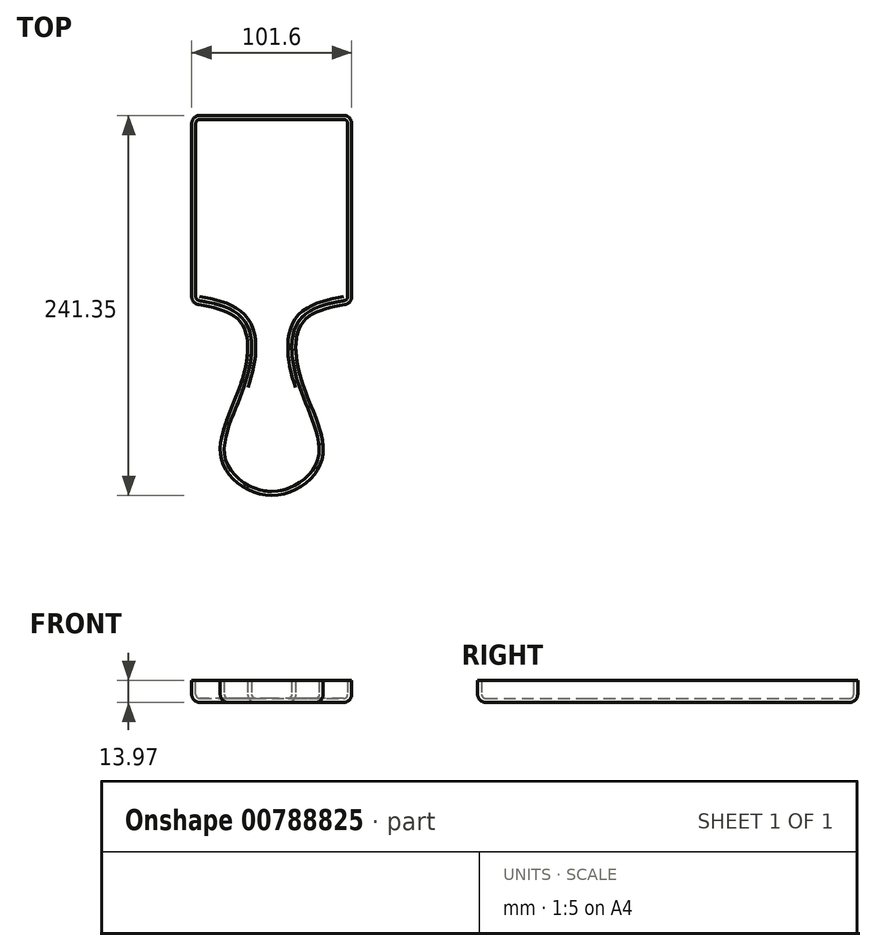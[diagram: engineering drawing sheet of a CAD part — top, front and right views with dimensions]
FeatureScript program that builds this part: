
annotation { "Feature Type Name" : "Feature", "Feature Type Description" : "" }
export const myFeature = defineFeature(function(context is Context, id is Id, definition is map)
    precondition{}
    {
        {
            var Q0;
            Q0=qCreatedBy(makeId("Top.planeOp"),FACE);
            var sketch = newSketch(context, id + "F0", { "sketchPlane" : qUnion([Q0])});
            skLineSegment(sketch, "E0.top", {"start": v(-50.8, -59.7) * mm, "end": v(50.8, -59.7) * mm});
            skLineSegment(sketch, "E1.bottom", {"start": v(-19.05, -59.7) * mm, "end": v(19.05, -59.7) * mm});
            skLineSegment(sketch, "E1.top", {"start": v(-19.05, -143.51) * mm, "end": v(19.05, -143.51) * mm});
            skLineSegment(sketch, "E2", {"start": v(-19.05, -59.69) * mm, "end": v(-138.22, -148.68) * mm, "construction": true});
            skPoint(sketch, "E3.4.internal.snap0", {"position": v(0, -143.51) * mm});
            skFitSpline(sketch, "E4", {"points": [v(31.98, -161.28) * mm, v(-138.22, -161.28) * mm], "startDerivative": vector(-191.75, -9.7) * mm, "endDerivative": vector(-168.23, 0) * mm, "construction": true});
            skFitSpline(sketch, "E5", {"points": [v(19.04, -111.52) * mm, v(-199.9, -111.52) * mm], "startDerivative": vector(-218.94, 0) * mm, "endDerivative": vector(-218.94, 0) * mm, "construction": true});
            skLineSegment(sketch, "E6", {"start": v(50.8, -59.7) * mm, "end": v(50.8, -228.04) * mm, "construction": true});
            skLineSegment(sketch, "E7", {"start": v(-50.8, -59.7) * mm, "end": v(-50.8, -228.04) * mm, "construction": true});
            skPoint(sketch, "E8", {"position": v(-44.45, -162.64) * mm});
            skPoint(sketch, "E9", {"position": v(31.8, -161.3) * mm});
            skLineSegment(sketch, "E10", {"start": v(0, -228.04) * mm, "end": v(0, -135.28) * mm});
            skPoint(sketch, "E11.orphan", {"position": v(0, -221.87) * mm});
            skLineSegment(sketch, "E12", {"start": v(-50.8, -59.7) * mm, "end": v(-50.8, 59.69) * mm});
            skLineSegment(sketch, "E13", {"start": v(-50.8, 59.69) * mm, "end": v(50.8, 59.69) * mm});
            skLineSegment(sketch, "E14", {"start": v(50.8, 59.69) * mm, "end": v(50.8, -59.7) * mm});
            skLineSegment(sketch, "E15", {"start": v(0, -59.7) * mm, "end": v(0, 0) * mm, "construction": true});
            skFitSpline(sketch, "E16", {"points": [v(19.04, -111.52) * mm, v(-199.9, -111.52) * mm], "startDerivative": vector(-218.94, 0) * mm, "endDerivative": vector(-218.94, 0) * mm, "construction": true});
            skFitSpline(sketch, "E17", {"points": [v(-50.8, -59.7) * mm, v(-19.83, -71.53) * mm, v(-19.05, -108.97) * mm, v(-31.95, -158.73) * mm, v(0, -181.66) * mm, v(31.95, -158.73) * mm, v(19.05, -108.97) * mm, v(19.83, -71.53) * mm, v(50.8, -59.7) * mm], "startDerivative": vector(328.9, -55.01) * mm, "endDerivative": vector(328.9, 55.01) * mm});
            skFitSpline(sketch, "E18.MirrorCS", {"points": [v(50.8, -59.7) * mm, v(19.83, -71.53) * mm, v(19.05, -108.97) * mm, v(31.95, -158.73) * mm, v(0, -181.66) * mm, v(-31.95, -158.73) * mm, v(-19.05, -108.97) * mm, v(-19.83, -71.53) * mm, v(-50.8, -59.7) * mm], "startDerivative": vector(-328.9, -55.01) * mm, "endDerivative": vector(-328.9, 55.01) * mm});
            skFitSpline(sketch, "E19", {"points": [v(-20.16, -129.65) * mm, v(-15.25, -116.48) * mm, v(-19.9, -111.52) * mm], "startDerivative": vector(14.14, 25.35) * mm, "endDerivative": vector(-15.4, 9.99) * mm});
            skFitSpline(sketch, "E20.MirrorCS", {"points": [v(20.16, -129.65) * mm, v(15.25, -116.48) * mm, v(19.9, -111.52) * mm], "startDerivative": vector(-14.14, 25.35) * mm, "endDerivative": vector(15.4, 9.99) * mm});
            skArc(sketch, "E21", {"start": v(-20.16, -129.65) * mm, "mid": v(0, -167.4) * mm, "end": v(20.16, -129.65) * mm});
            skLineSegment(sketch, "E22", {"start": v(-15.25, -116.48) * mm, "end": v(-15.25, -59.7) * mm});
            skSolve(sketch);
        }
        {
            var Q0;
            Q0 = qSketchRegion(id + "F0", true);
            extrude(context, id + "F1", {"entities" : qUnion([Q0]), "depth" : 19.05 * mm, "offsetDistance" : 25.4 * mm});
        }
        {
            var Q0;
            Q0=makeQuery(id+"F1.opExtrude","CAP_EDGE",EDGE,{"disambiguationData":[OSD([sQuery(id+"F0.wireOp",EDGE,"E0.left")])],"isStart":false});
            var Q1;
            {var subQ0=sQuery(id+"F0.wireOp",EDGE,"E0.top");Q1=makeQuery(id+"F1.opExtrude","CAP_EDGE",EDGE,{"disambiguationData":[OSD([subQ0]),TDD([makeQuery(id+"F0.imprint","IMPRINT",EDGE,{"disambiguationData":[TD([[makeQuery(id+"F0.imprint","INTERSECT",VERTEX,{"derivedFrom":[subQ0,sQuery(id+"F0.wireOp",EDGE,"E0.left")]}),-1.0]])],"derivedFrom":subQ0})])],"isStart":false});}
            var Q2;
            {var subQ0=sQuery(id+"F0.wireOp",EDGE,"E0.top");Q2=makeQuery(id+"F1.opExtrude","CAP_EDGE",EDGE,{"disambiguationData":[OSD([subQ0]),TDD([makeQuery(id+"F0.imprint","IMPRINT",EDGE,{"disambiguationData":[TD([[makeQuery(id+"F0.imprint","INTERSECT",VERTEX,{"derivedFrom":[subQ0,sQuery(id+"F0.wireOp",EDGE,"E0.left")]}),-1.0]])],"derivedFrom":subQ0})])],"isStart":true});}
            var Q3;
            Q3=makeQuery(id+"F1.opExtrude","CAP_EDGE",EDGE,{"disambiguationData":[OSD([sQuery(id+"F0.wireOp",EDGE,"E0.left")])],"isStart":true});
            var Q4;
            Q4=makeQuery(id+"F1.opExtrude","SWEPT_EDGE",EDGE,{"disambiguationData":[OSD([sQuery(id+"F0.wireOp",EDGE,"E0.top"),sQuery(id+"F0.wireOp",EDGE,"E0.left")])]});
            var Q5;
            Q5=makeQuery(id+"F1.opExtrude","SWEPT_EDGE",EDGE,{"disambiguationData":[OSD([sQuery(id+"F0.wireOp",EDGE,"E0.top"),sQuery(id+"F0.wireOp",EDGE,"E1.bottom"),sQuery(id+"F0.wireOp",EDGE,"E1.left")])]});
            var Q6;
            Q6=makeQuery(id+"F1.opExtrude","CAP_EDGE",EDGE,{"disambiguationData":[OSD([sQuery(id+"F0.wireOp",EDGE,"E0.bottom")])],"isStart":false});
            var Q7;
            Q7=makeQuery(id+"F1.opExtrude","CAP_EDGE",EDGE,{"disambiguationData":[OSD([sQuery(id+"F0.wireOp",EDGE,"E0.right")])],"isStart":false});
            var Q8;
            {var subQ0=sQuery(id+"F0.wireOp",EDGE,"E0.top");Q8=makeQuery(id+"F1.opExtrude","CAP_EDGE",EDGE,{"disambiguationData":[OSD([subQ0]),TDD([makeQuery(id+"F0.imprint","IMPRINT",EDGE,{"disambiguationData":[TD([[makeQuery(id+"F0.imprint","INTERSECT",VERTEX,{"derivedFrom":[subQ0,sQuery(id+"F0.wireOp",EDGE,"E0.right")]}),1.0]])],"derivedFrom":subQ0})])],"isStart":false});}
            var Q9;
            Q9=makeQuery(id+"F1.opExtrude","CAP_EDGE",EDGE,{"disambiguationData":[OSD([sQuery(id+"F0.wireOp",EDGE,"E1.right")])],"isStart":false});
            var Q10;
            Q10=makeQuery(id+"F1.opExtrude","CAP_EDGE",EDGE,{"disambiguationData":[OSD([sQuery(id+"F0.wireOp",EDGE,"E1.top")])],"isStart":false});
            var Q11;
            Q11=makeQuery(id+"F1.opExtrude","SWEPT_EDGE",EDGE,{"disambiguationData":[OSD([sQuery(id+"F0.wireOp",EDGE,"E1.top"),sQuery(id+"F0.wireOp",EDGE,"E1.right")])]});
            var Q12;
            Q12=makeQuery(id+"F1.opExtrude","SWEPT_EDGE",EDGE,{"disambiguationData":[OSD([sQuery(id+"F0.wireOp",EDGE,"E1.top"),sQuery(id+"F0.wireOp",EDGE,"E1.left")])]});
            var Q13;
            Q13=makeQuery(id+"F1.opExtrude","SWEPT_EDGE",EDGE,{"disambiguationData":[OSD([sQuery(id+"F0.wireOp",EDGE,"E0.top"),sQuery(id+"F0.wireOp",EDGE,"E1.bottom"),sQuery(id+"F0.wireOp",EDGE,"E1.right")])]});
            var Q14;
            Q14=makeQuery(id+"F1.opExtrude","SWEPT_EDGE",EDGE,{"disambiguationData":[OSD([sQuery(id+"F0.wireOp",EDGE,"E0.top"),sQuery(id+"F0.wireOp",EDGE,"E0.right")])]});
            var Q15;
            Q15=makeQuery(id+"F1.opExtrude","SWEPT_EDGE",EDGE,{"disambiguationData":[OSD([sQuery(id+"F0.wireOp",EDGE,"E0.bottom"),sQuery(id+"F0.wireOp",EDGE,"E0.right")])]});
            var Q16;
            Q16=makeQuery(id+"F1.opExtrude","CAP_EDGE",EDGE,{"disambiguationData":[OSD([sQuery(id+"F0.wireOp",EDGE,"E0.right")])],"isStart":true});
            var Q17;
            {var subQ0=sQuery(id+"F0.wireOp",EDGE,"E0.top");Q17=makeQuery(id+"F1.opExtrude","CAP_EDGE",EDGE,{"disambiguationData":[OSD([subQ0]),TDD([makeQuery(id+"F0.imprint","IMPRINT",EDGE,{"disambiguationData":[TD([[makeQuery(id+"F0.imprint","INTERSECT",VERTEX,{"derivedFrom":[subQ0,sQuery(id+"F0.wireOp",EDGE,"E0.right")]}),1.0]])],"derivedFrom":subQ0})])],"isStart":true});}
            var Q18;
            Q18=makeQuery(id+"F1.opExtrude","CAP_EDGE",EDGE,{"disambiguationData":[OSD([sQuery(id+"F0.wireOp",EDGE,"E1.right")])],"isStart":true});
            var Q19;
            Q19=makeQuery(id+"F1.opExtrude","CAP_EDGE",EDGE,{"disambiguationData":[OSD([sQuery(id+"F0.wireOp",EDGE,"E1.top")])],"isStart":true});
            var Q20;
            Q20=makeQuery(id+"F1.opExtrude","CAP_EDGE",EDGE,{"disambiguationData":[OSD([sQuery(id+"F0.wireOp",EDGE,"E0.bottom")])],"isStart":true});
            var Q21;
            Q21=makeQuery(id+"F1.opExtrude","SWEPT_EDGE",EDGE,{"disambiguationData":[OSD([sQuery(id+"F0.wireOp",EDGE,"E0.bottom"),sQuery(id+"F0.wireOp",EDGE,"E0.left")])]});
            var Q22;
            Q22=makeQuery(id+"F1.opExtrude","CAP_EDGE",EDGE,{"disambiguationData":[OSD([sQuery(id+"F0.wireOp",EDGE,"4c1d50d4-069b-4383-b718-4d861729b4e2")])],"isStart":false});
            var Q23;
            Q23=makeQuery(id+"F1.opExtrude","CAP_EDGE",EDGE,{"disambiguationData":[OSD([sQuery(id+"F0.wireOp",EDGE,"4c1d50d4-069b-4383-b718-4d861729b4e2")])],"isStart":true});
            var Q24;
            Q24=makeQuery(id+"F1.opExtrude","CAP_EDGE",EDGE,{"disambiguationData":[OSD([sQuery(id+"F0.wireOp",EDGE,"fae6d164-7b8f-4678-8160-efaf614075e90.MirrorCS")])],"isStart":false});
            var Q25;
            Q25=makeQuery(id+"F1.opExtrude","CAP_EDGE",EDGE,{"disambiguationData":[OSD([sQuery(id+"F0.wireOp",EDGE,"d6001748-2b6a-4d9c-a908-10d513fc31c9")])],"isStart":false});
            var Q26;
            Q26=makeQuery(id+"F1.opExtrude","CAP_EDGE",EDGE,{"disambiguationData":[OSD([sQuery(id+"F0.wireOp",EDGE,"d6001748-2b6a-4d9c-a908-10d513fc31c9")])],"isStart":true});
            var Q27;
            Q27=makeQuery(id+"F1.opExtrude","SWEPT_EDGE",EDGE,{"disambiguationData":[OSD([sQuery(id+"F0.wireOp",EDGE,"d6001748-2b6a-4d9c-a908-10d513fc31c9"),sQuery(id+"F0.wireOp",EDGE,"fae6d164-7b8f-4678-8160-efaf614075e90.MirrorCS")])]});
            var Q28;
            Q28=makeQuery(id+"F1.opExtrude","CAP_EDGE",EDGE,{"disambiguationData":[OSD([sQuery(id+"F0.wireOp",EDGE,"8a59b3ed-8c03-450e-87c2-30eb3ba6beeb0.MirrorCS")])],"isStart":false});
            var Q29;
            Q29=makeQuery(id+"F1.opExtrude","CAP_EDGE",EDGE,{"disambiguationData":[OSD([sQuery(id+"F0.wireOp",EDGE,"ede2a839-0906-4238-8b5b-b33d8fcfbcd3")])],"isStart":true});
            var Q30;
            Q30=makeQuery(id+"F1.opExtrude","CAP_EDGE",EDGE,{"disambiguationData":[OSD([sQuery(id+"F0.wireOp",EDGE,"ede2a839-0906-4238-8b5b-b33d8fcfbcd3")])],"isStart":false});
            var Q31;
            Q31=makeQuery(id+"F1.opExtrude","CAP_EDGE",EDGE,{"disambiguationData":[OSD([sQuery(id+"F0.wireOp",EDGE,"8a59b3ed-8c03-450e-87c2-30eb3ba6beeb0.MirrorCS")])],"isStart":true});
            var Q32;
            Q32=makeQuery(id+"F1.opExtrude","CAP_EDGE",EDGE,{"disambiguationData":[OSD([sQuery(id+"F0.wireOp",EDGE,"E14")])],"isStart":true});
            var Q33;
            Q33=makeQuery(id+"F1.opExtrude","CAP_EDGE",EDGE,{"disambiguationData":[OSD([sQuery(id+"F0.wireOp",EDGE,"E14")])],"isStart":false});
            var Q34;
            Q34=makeQuery(id+"F1.opExtrude","SWEPT_EDGE",EDGE,{"disambiguationData":[OSD([sQuery(id+"F0.wireOp",EDGE,"E13"),sQuery(id+"F0.wireOp",EDGE,"E14")])]});
            var Q35;
            Q35=makeQuery(id+"F1.opExtrude","SWEPT_EDGE",EDGE,{"disambiguationData":[OSD([sQuery(id+"F0.wireOp",EDGE,"E12"),sQuery(id+"F0.wireOp",EDGE,"E13")])]});
            var Q36;
            Q36=makeQuery(id+"F1.opExtrude","CAP_EDGE",EDGE,{"disambiguationData":[OSD([sQuery(id+"F0.wireOp",EDGE,"E13")])],"isStart":true});
            var Q37;
            Q37=makeQuery(id+"F1.opExtrude","CAP_EDGE",EDGE,{"disambiguationData":[OSD([sQuery(id+"F0.wireOp",EDGE,"E13")])],"isStart":false});
            var Q38;
            Q38=makeQuery(id+"F1.opExtrude","CAP_EDGE",EDGE,{"disambiguationData":[OSD([sQuery(id+"F0.wireOp",EDGE,"E12")])],"isStart":false});
            var Q39;
            Q39=makeQuery(id+"F1.opExtrude","CAP_EDGE",EDGE,{"disambiguationData":[OSD([sQuery(id+"F0.wireOp",EDGE,"E12")])],"isStart":true});
            var Q40;
            Q40=makeQuery(id+"F1.opExtrude","CAP_EDGE",EDGE,{"disambiguationData":[OSD([sQuery(id+"F0.wireOp",EDGE,"a16801fe-df26-48e4-8f01-7dd2797d49e1"),sQuery(id+"F0.wireOp",EDGE,"96520f5b-7c93-41a4-aa58-d3013fd5ee490.MirrorCS")])],"isStart":false});
            var Q41;
            Q41=makeQuery(id+"F1.opExtrude","CAP_EDGE",EDGE,{"disambiguationData":[OSD([sQuery(id+"F0.wireOp",EDGE,"a16801fe-df26-48e4-8f01-7dd2797d49e1"),sQuery(id+"F0.wireOp",EDGE,"96520f5b-7c93-41a4-aa58-d3013fd5ee490.MirrorCS")])],"isStart":true});
            var Q42;
            Q42=makeQuery(id+"F1.opExtrude","CAP_EDGE",EDGE,{"disambiguationData":[OSD([sQuery(id+"F0.wireOp",EDGE,"E21")])],"isStart":false});
            var Q43;
            Q43=makeQuery(id+"F1.opExtrude","CAP_EDGE",EDGE,{"disambiguationData":[OSD([sQuery(id+"F0.wireOp",EDGE,"E18.MirrorCS")])],"isStart":false});
            var Q44;
            Q44=makeQuery(id+"F1.opExtrude","CAP_EDGE",EDGE,{"disambiguationData":[OSD([sQuery(id+"F0.wireOp",EDGE,"E17")])],"isStart":false});
            var Q45;
            Q45=makeQuery(id+"F1.opExtrude","SWEPT_EDGE",EDGE,{"disambiguationData":[OSD([sQuery(id+"F0.wireOp",EDGE,"E18.MirrorCS"),sQuery(id+"F0.wireOp",EDGE,"E20.MirrorCS")])]});
            var Q46;
            Q46=makeQuery(id+"F1.opExtrude","SWEPT_EDGE",EDGE,{"disambiguationData":[OSD([sQuery(id+"F0.wireOp",EDGE,"E20.MirrorCS"),sQuery(id+"F0.wireOp",EDGE,"E21")])]});
            var Q47;
            Q47=makeQuery(id+"F1.opExtrude","CAP_EDGE",EDGE,{"disambiguationData":[OSD([sQuery(id+"F0.wireOp",EDGE,"E20.MirrorCS")])],"isStart":true});
            var Q48;
            Q48=makeQuery(id+"F1.opExtrude","CAP_EDGE",EDGE,{"disambiguationData":[OSD([sQuery(id+"F0.wireOp",EDGE,"E18.MirrorCS")])],"isStart":true});
            var Q49;
            Q49=makeQuery(id+"F1.opExtrude","CAP_EDGE",EDGE,{"disambiguationData":[OSD([sQuery(id+"F0.wireOp",EDGE,"E17")])],"isStart":true});
            var Q50;
            Q50=makeQuery(id+"F1.opExtrude","SWEPT_EDGE",EDGE,{"disambiguationData":[OSD([sQuery(id+"F0.wireOp",EDGE,"E17"),sQuery(id+"F0.wireOp",EDGE,"E19")])]});
            var Q51;
            Q51=makeQuery(id+"F1.opExtrude","SWEPT_EDGE",EDGE,{"disambiguationData":[OSD([sQuery(id+"F0.wireOp",EDGE,"E19"),sQuery(id+"F0.wireOp",EDGE,"E21")])]});
            var Q52;
            Q52=makeQuery(id+"F1.opExtrude","CAP_EDGE",EDGE,{"disambiguationData":[OSD([sQuery(id+"F0.wireOp",EDGE,"E19")])],"isStart":false});
            var Q53;
            Q53=makeQuery(id+"F1.opExtrude","CAP_EDGE",EDGE,{"disambiguationData":[OSD([sQuery(id+"F0.wireOp",EDGE,"E20.MirrorCS")])],"isStart":false});
            fillet(context, id + "F2", {"entities" : qUnion([Q0, Q1, Q2, Q3, Q4, Q5, Q6, Q7, Q8, Q9, Q10, Q11, Q12, Q13, Q14, Q15, Q16, Q17, Q18, Q19, Q20, Q21, Q22, Q23, Q24, Q25, Q26, Q27, Q28, Q29, Q30, Q31, Q32, Q33, Q34, Q35, Q36, Q37, Q38, Q39, Q40, Q41, Q42, Q43, Q44, Q45, Q46, Q47, Q48, Q49, Q50, Q51, Q52, Q53]), "radius" : 5.08 * mm, "tangentPropagation" : true, "allowEdgeOverflow" : false});
        }
        {
            var Q0;
            {var subQ0=sQuery(id+"F0.wireOp",EDGE,"E14");var subQ1=sQuery(id+"F0.wireOp",EDGE,"8a59b3ed-8c03-450e-87c2-30eb3ba6beeb0.MirrorCS");var subQ2=sQuery(id+"F0.wireOp",EDGE,"E0.top");Q0=makeQuery(id+"F2.opFillet","BLEND_FACE",FACE,{"disambiguationData":[OSD([subQ2,subQ1,subQ0]),TDD([makeQuery(id+"F1.opExtrude","CAP_VERTEX",VERTEX,{"disambiguationData":[OSD([subQ2,subQ1,subQ0])],"isStart":false})])]});}
            var Q1;
            Q1=makeQuery(id+"F1.opExtrude","CAP_FACE",FACE,{"disambiguationData":[OSD([sQuery(id+"F0.wireOp",EDGE,"ede2a839-0906-4238-8b5b-b33d8fcfbcd3"),sQuery(id+"F0.wireOp",EDGE,"8a59b3ed-8c03-450e-87c2-30eb3ba6beeb0.MirrorCS"),sQuery(id+"F0.wireOp",EDGE,"E12"),sQuery(id+"F0.wireOp",EDGE,"E13"),sQuery(id+"F0.wireOp",EDGE,"E14")])],"isStart":false});
            var Q2;
            {var subQ0=sQuery(id+"F0.wireOp",EDGE,"ede2a839-0906-4238-8b5b-b33d8fcfbcd3");Q2=makeQuery(id+"F2.opFillet","BLEND_FACE",FACE,{"disambiguationData":[OSD([subQ0]),TDD([makeQuery(id+"F1.opExtrude","CAP_EDGE",EDGE,{"disambiguationData":[OSD([subQ0])],"isStart":false})])]});}
            var Q3;
            {var subQ0=sQuery(id+"F0.wireOp",EDGE,"E12");Q3=makeQuery(id+"F2.opFillet","BLEND_FACE",FACE,{"disambiguationData":[OSD([subQ0]),TDD([makeQuery(id+"F1.opExtrude","CAP_EDGE",EDGE,{"disambiguationData":[OSD([subQ0])],"isStart":false})])]});}
            var Q4;
            {var subQ0=sQuery(id+"F0.wireOp",EDGE,"8a59b3ed-8c03-450e-87c2-30eb3ba6beeb0.MirrorCS");Q4=makeQuery(id+"F2.opFillet","BLEND_FACE",FACE,{"disambiguationData":[OSD([subQ0]),TDD([makeQuery(id+"F1.opExtrude","CAP_EDGE",EDGE,{"disambiguationData":[OSD([subQ0])],"isStart":false})])]});}
            var Q5;
            {var subQ0=sQuery(id+"F0.wireOp",EDGE,"E14");Q5=makeQuery(id+"F2.opFillet","BLEND_FACE",FACE,{"disambiguationData":[OSD([subQ0]),TDD([makeQuery(id+"F1.opExtrude","CAP_EDGE",EDGE,{"disambiguationData":[OSD([subQ0])],"isStart":false})])]});}
            var Q6;
            {var subQ0=sQuery(id+"F0.wireOp",EDGE,"E13");Q6=makeQuery(id+"F2.opFillet","BLEND_FACE",FACE,{"disambiguationData":[OSD([subQ0]),TDD([makeQuery(id+"F1.opExtrude","CAP_EDGE",EDGE,{"disambiguationData":[OSD([subQ0])],"isStart":false})])]});}
            var Q7;
            {var subQ0=sQuery(id+"F0.wireOp",EDGE,"E14");var subQ1=sQuery(id+"F0.wireOp",EDGE,"E13");Q7=makeQuery(id+"F2.opFillet","BLEND_FACE",FACE,{"disambiguationData":[OSD([subQ1,subQ0]),TDD([makeQuery(id+"F1.opExtrude","CAP_VERTEX",VERTEX,{"disambiguationData":[OSD([subQ1,subQ0])],"isStart":false})])]});}
            var Q8;
            {var subQ0=sQuery(id+"F0.wireOp",EDGE,"E12");var subQ1=sQuery(id+"F0.wireOp",EDGE,"ede2a839-0906-4238-8b5b-b33d8fcfbcd3");var subQ2=sQuery(id+"F0.wireOp",EDGE,"E0.top");Q8=makeQuery(id+"F2.opFillet","BLEND_FACE",FACE,{"disambiguationData":[OSD([subQ2,subQ1,subQ0]),TDD([makeQuery(id+"F1.opExtrude","CAP_VERTEX",VERTEX,{"disambiguationData":[OSD([subQ2,subQ1,subQ0])],"isStart":false})])]});}
            var Q9;
            {var subQ0=sQuery(id+"F0.wireOp",EDGE,"E13");var subQ1=sQuery(id+"F0.wireOp",EDGE,"E12");Q9=makeQuery(id+"F2.opFillet","BLEND_FACE",FACE,{"disambiguationData":[OSD([subQ1,subQ0]),TDD([makeQuery(id+"F1.opExtrude","CAP_VERTEX",VERTEX,{"disambiguationData":[OSD([subQ1,subQ0])],"isStart":false})])]});}
            var Q10;
            {var subQ0=sQuery(id+"F0.wireOp",EDGE,"96520f5b-7c93-41a4-aa58-d3013fd5ee490.MirrorCS");var subQ1=sQuery(id+"F0.wireOp",EDGE,"a16801fe-df26-48e4-8f01-7dd2797d49e1");Q10=makeQuery(id+"F2.opFillet","BLEND_FACE",FACE,{"disambiguationData":[OSD([subQ1,subQ0]),TDD([makeQuery(id+"F1.opExtrude","CAP_EDGE",EDGE,{"disambiguationData":[OSD([subQ1,subQ0])],"isStart":false})])]});}
            var Q11;
            {var subQ0=sQuery(id+"F0.wireOp",EDGE,"E21");Q11=makeQuery(id+"F2.opFillet","BLEND_FACE",FACE,{"disambiguationData":[OSD([subQ0]),TDD([makeQuery(id+"F1.opExtrude","CAP_EDGE",EDGE,{"disambiguationData":[OSD([subQ0])],"isStart":false})])]});}
            var Q12;
            {var subQ0=sQuery(id+"F0.wireOp",EDGE,"E19");Q12=makeQuery(id+"F2.opFillet","BLEND_FACE",FACE,{"disambiguationData":[OSD([subQ0]),TDD([makeQuery(id+"F1.opExtrude","CAP_EDGE",EDGE,{"disambiguationData":[OSD([subQ0])],"isStart":false})])]});}
            var Q13;
            {var subQ0=sQuery(id+"F0.wireOp",EDGE,"E20.MirrorCS");Q13=makeQuery(id+"F2.opFillet","BLEND_FACE",FACE,{"disambiguationData":[OSD([subQ0]),TDD([makeQuery(id+"F1.opExtrude","CAP_EDGE",EDGE,{"disambiguationData":[OSD([subQ0])],"isStart":false})])]});}
            var Q14;
            {var subQ0=sQuery(id+"F0.wireOp",EDGE,"E17");Q14=makeQuery(id+"F2.opFillet","BLEND_FACE",FACE,{"disambiguationData":[OSD([subQ0]),TDD([makeQuery(id+"F1.opExtrude","CAP_EDGE",EDGE,{"disambiguationData":[OSD([subQ0])],"isStart":false})])]});}
            var Q15;
            {var subQ0=sQuery(id+"F0.wireOp",EDGE,"E18.MirrorCS");Q15=makeQuery(id+"F2.opFillet","BLEND_FACE",FACE,{"disambiguationData":[OSD([subQ0]),TDD([makeQuery(id+"F1.opExtrude","CAP_EDGE",EDGE,{"disambiguationData":[OSD([subQ0])],"isStart":false})])]});}
            var Q16;
            {var subQ0=sQuery(id+"F0.wireOp",EDGE,"E20.MirrorCS");var subQ1=sQuery(id+"F0.wireOp",EDGE,"E18.MirrorCS");Q16=makeQuery(id+"F2.opFillet","BLEND_FACE",FACE,{"disambiguationData":[OSD([subQ1,subQ0]),TDD([makeQuery(id+"F1.opExtrude","CAP_VERTEX",VERTEX,{"disambiguationData":[OSD([subQ1,subQ0])],"isStart":false})])]});}
            var Q17;
            {var subQ0=sQuery(id+"F0.wireOp",EDGE,"E19");var subQ1=sQuery(id+"F0.wireOp",EDGE,"E17");Q17=makeQuery(id+"F2.opFillet","BLEND_FACE",FACE,{"disambiguationData":[OSD([subQ1,subQ0]),TDD([makeQuery(id+"F1.opExtrude","CAP_VERTEX",VERTEX,{"disambiguationData":[OSD([subQ1,subQ0])],"isStart":false})])]});}
            var Q18;
            {var subQ0=sQuery(id+"F0.wireOp",EDGE,"E21");var subQ1=sQuery(id+"F0.wireOp",EDGE,"E19");Q18=makeQuery(id+"F2.opFillet","BLEND_FACE",FACE,{"disambiguationData":[OSD([subQ1,subQ0]),TDD([makeQuery(id+"F1.opExtrude","CAP_VERTEX",VERTEX,{"disambiguationData":[OSD([subQ1,subQ0])],"isStart":false})])]});}
            var Q19;
            {var subQ0=sQuery(id+"F0.wireOp",EDGE,"E21");var subQ1=sQuery(id+"F0.wireOp",EDGE,"E20.MirrorCS");Q19=makeQuery(id+"F2.opFillet","BLEND_FACE",FACE,{"disambiguationData":[OSD([subQ1,subQ0]),TDD([makeQuery(id+"F1.opExtrude","CAP_VERTEX",VERTEX,{"disambiguationData":[OSD([subQ1,subQ0])],"isStart":false})])]});}
            shell(context, id + "F3", {"entities" : qUnion([Q0, Q1, Q2, Q3, Q4, Q5, Q6, Q7, Q8, Q9, Q10, Q11, Q12, Q13, Q14, Q15, Q16, Q17, Q18, Q19]), "thickness" : 2.54 * mm});
        }
    });
